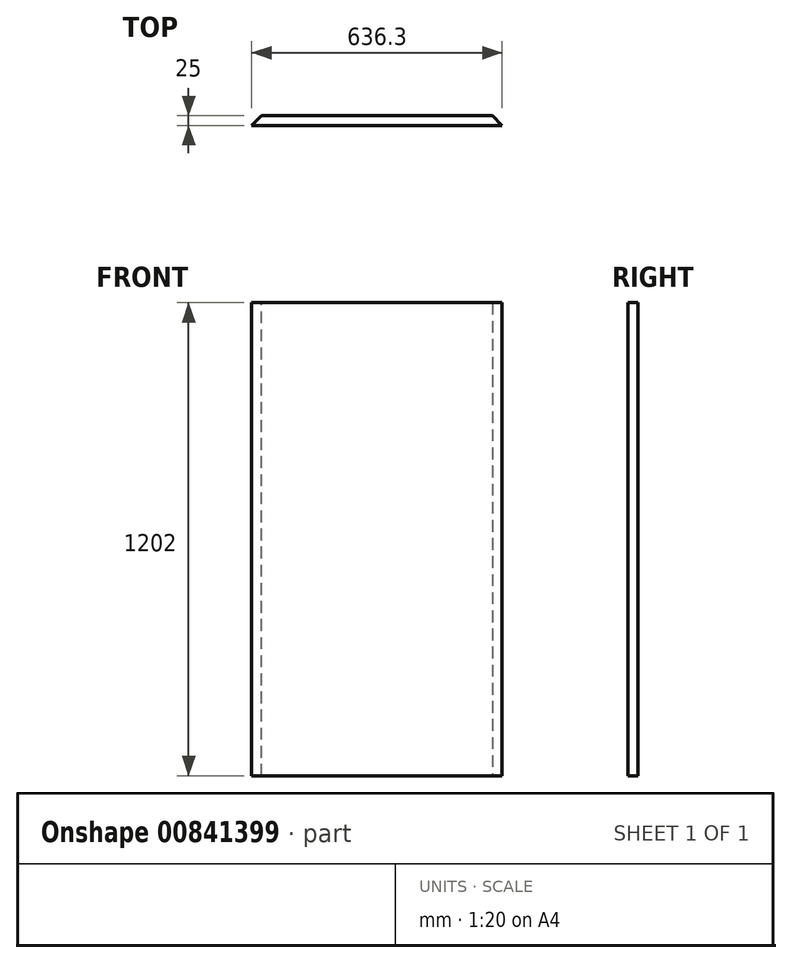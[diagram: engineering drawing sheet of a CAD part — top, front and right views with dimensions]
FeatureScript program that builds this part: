
annotation { "Feature Type Name" : "Feature", "Feature Type Description" : "" }
export const myFeature = defineFeature(function(context is Context, id is Id, definition is map)
    precondition{}
    {
        {
            var Q0;
            Q0=qCreatedBy(makeId("Front.planeOp"),FACE);
            var sketch = newSketch(context, id + "F0", { "sketchPlane" : qUnion([Q0])});
            skLineSegment(sketch, "E0.bottom", {"start": v(0, 0) * mm, "end": v(636.3, 0) * mm});
            skLineSegment(sketch, "E0.top", {"start": v(0, 1202) * mm, "end": v(636.3, 1202) * mm});
            skLineSegment(sketch, "E0.left", {"start": v(0, 0) * mm, "end": v(0, 1202) * mm});
            skLineSegment(sketch, "E0.right", {"start": v(636.3, 0) * mm, "end": v(636.3, 1202) * mm});
            skSolve(sketch);
        }
        {
            var Q0;
            Q0 = qSketchRegion(id + "F0", true);
            extrude(context, id + "F1", {"entities" : qUnion([Q0]), "depth" : 25 * mm, "offsetDistance" : 25 * mm});
        }
        {
            var Q0;
            Q0=makeQuery(id+"F1.opExtrude","CAP_EDGE",EDGE,{"disambiguationData":[OSD([sQuery(id+"F0.wireOp",EDGE,"E0.right")])],"isStart":true});
            var Q1;
            Q1=makeQuery(id+"F1.opExtrude","CAP_EDGE",EDGE,{"disambiguationData":[OSD([sQuery(id+"F0.wireOp",EDGE,"E0.left")])],"isStart":true});
            chamfer(context, id + "F2", {"entities" : qUnion([Q0, Q1]), "width" : 25 * mm, "tangentPropagation" : true});
        }
    });
